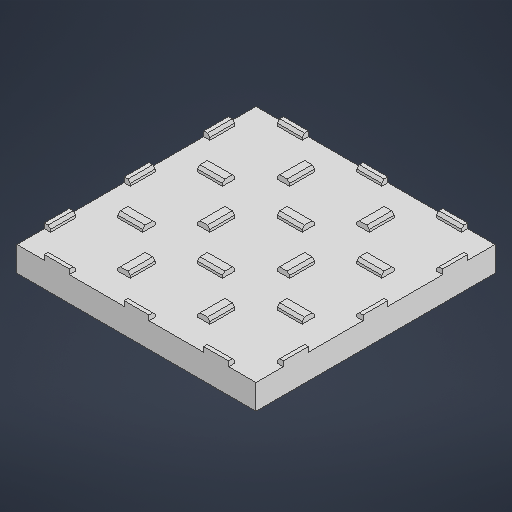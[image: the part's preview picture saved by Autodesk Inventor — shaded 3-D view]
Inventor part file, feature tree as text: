
AUTODESK INVENTOR PART (.ipt)
format: ipt  version: 2025.1 (Build 291241000, 241)  size: 693,248 bytes
history: native  units: mm
features: extrude x2, sketch x1, chamfer x1, pattern_linear x1
ambient origin geometry x8: Origin, YZ Plane, XZ Plane, XY Plane, X Axis, Y Axis, Z Axis, Center Point
bodies: Solid1 (feature_tree)
feature tree (5):
  sketch  "Sketch1"  dims[d0=32.0mm d3=10.0mm d4=10.0mm d5=0.0mm d6=2.0mm d7=0.0mm d8=25.4mm d10=27.0mm d11=30.0mm d13=32.0mm d14=30.0mm d16=32.0mm d17=1.0mm d18=2.0mm d19=45.0deg]
  extrude  "Extrusion1"  Depth=10.0mm
  extrude  "Extrusion2"  Depth=10.0mm TaperAngle=0.0deg
  chamfer  "Chamfer1"  Distance=2.0mm
  pattern_linear  "Rectangular Pattern1"  Spacing1=25.4mm  [1 undecoded]
note: 1 required parameter value undecoded (feature->parameter linkage not recoverable at this tier; creation-order binding heuristic only, values carry confidence <= 0.55)
